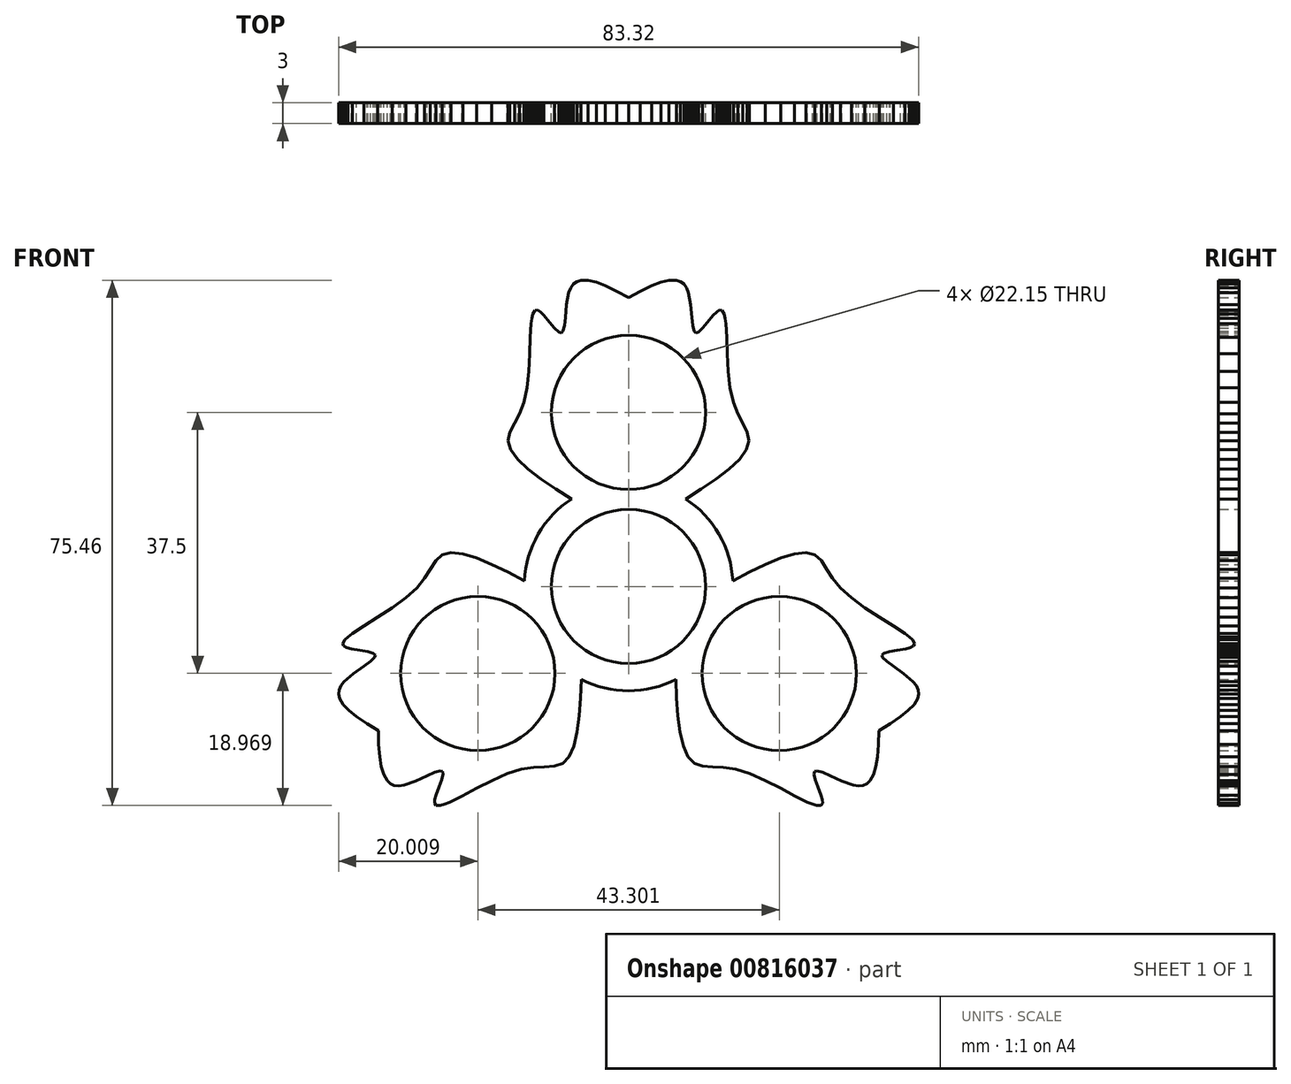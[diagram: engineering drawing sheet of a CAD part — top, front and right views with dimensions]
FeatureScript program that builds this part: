
annotation { "Feature Type Name" : "Feature", "Feature Type Description" : "" }
export const myFeature = defineFeature(function(context is Context, id is Id, definition is map)
    precondition{}
    {
        {
            var Q0;
            Q0=qCreatedBy(makeId("Front.planeOp"),FACE);
            var sketch = newSketch(context, id + "F0", { "sketchPlane" : qUnion([Q0])});
            skArc(sketch, "E0", {"start": v(0, -17.34) * mm, "mid": v(9.6, -11.8) * mm, "end": v(9.6, -0.72) * mm});
            skArc(sketch, "E1", {"start": v(9.6, -0.72) * mm, "mid": v(0, 4.81) * mm, "end": v(-9.6, -0.72) * mm});
            skArc(sketch, "E2", {"start": v(-9.6, -0.72) * mm, "mid": v(-9.6, -11.8) * mm, "end": v(0, -17.34) * mm});
            skLineSegment(sketch, "E3", {"start": v(0, 35.24) * mm, "end": v(-1.7, 36.16) * mm});
            skLineSegment(sketch, "E4", {"start": v(-1.7, 36.16) * mm, "end": v(-3.34, 36.95) * mm});
            skLineSegment(sketch, "E5", {"start": v(-3.34, 36.95) * mm, "end": v(-4.64, 37.45) * mm});
            skLineSegment(sketch, "E6", {"start": v(-4.64, 37.45) * mm, "end": v(-5.82, 37.73) * mm});
            skLineSegment(sketch, "E7", {"start": v(-5.82, 37.73) * mm, "end": v(-6.85, 37.73) * mm});
            skLineSegment(sketch, "E8", {"start": v(-6.85, 37.73) * mm, "end": v(-7.44, 37.55) * mm});
            skLineSegment(sketch, "E9", {"start": v(-7.44, 37.55) * mm, "end": v(-7.93, 37.2) * mm});
            skLineSegment(sketch, "E10", {"start": v(-7.93, 37.2) * mm, "end": v(-8.3, 36.67) * mm});
            skLineSegment(sketch, "E11", {"start": v(-8.3, 36.67) * mm, "end": v(-8.59, 35.96) * mm});
            skLineSegment(sketch, "E12", {"start": v(-8.59, 35.96) * mm, "end": v(-8.92, 34.22) * mm});
            skLineSegment(sketch, "E13", {"start": v(-8.92, 34.22) * mm, "end": v(-9.08, 32.4) * mm});
            skLineSegment(sketch, "E14", {"start": v(-9.08, 32.4) * mm, "end": v(-9.2, 31.24) * mm});
            skLineSegment(sketch, "E15", {"start": v(-9.2, 31.24) * mm, "end": v(-9.41, 30.44) * mm});
            skLineSegment(sketch, "E16", {"start": v(-9.41, 30.44) * mm, "end": v(-9.66, 30.18) * mm});
            skLineSegment(sketch, "E17", {"start": v(-9.66, 30.18) * mm, "end": v(-10.02, 30.29) * mm});
            skLineSegment(sketch, "E18", {"start": v(-10.02, 30.29) * mm, "end": v(-10.64, 30.86) * mm});
            skLineSegment(sketch, "E19", {"start": v(-10.64, 30.86) * mm, "end": v(-11.34, 31.71) * mm});
            skLineSegment(sketch, "E20", {"start": v(-11.34, 31.71) * mm, "end": v(-12.15, 32.69) * mm});
            skLineSegment(sketch, "E21", {"start": v(-12.15, 32.69) * mm, "end": v(-12.63, 33.18) * mm});
            skLineSegment(sketch, "E22", {"start": v(-12.63, 33.18) * mm, "end": v(-13.05, 33.45) * mm});
            skLineSegment(sketch, "E23", {"start": v(-13.05, 33.45) * mm, "end": v(-13.41, 33.42) * mm});
            skLineSegment(sketch, "E24", {"start": v(-13.41, 33.42) * mm, "end": v(-13.75, 32.88) * mm});
            skLineSegment(sketch, "E25", {"start": v(-13.75, 32.88) * mm, "end": v(-13.9, 32.27) * mm});
            skLineSegment(sketch, "E26", {"start": v(-13.9, 32.27) * mm, "end": v(-14, 31.5) * mm});
            skLineSegment(sketch, "E27", {"start": v(-14, 31.5) * mm, "end": v(-14.12, 29.5) * mm});
            skLineSegment(sketch, "E28", {"start": v(-14.12, 29.5) * mm, "end": v(-14.2, 27.15) * mm});
            skLineSegment(sketch, "E29", {"start": v(-14.2, 27.15) * mm, "end": v(-14.33, 24.67) * mm});
            skLineSegment(sketch, "E30", {"start": v(-14.33, 24.67) * mm, "end": v(-14.58, 22.27) * mm});
            skLineSegment(sketch, "E31", {"start": v(-14.58, 22.27) * mm, "end": v(-15.04, 20.2) * mm});
            skLineSegment(sketch, "E32", {"start": v(-15.04, 20.2) * mm, "end": v(-15.69, 18.53) * mm});
            skLineSegment(sketch, "E33", {"start": v(-15.69, 18.53) * mm, "end": v(-16.38, 17.18) * mm});
            skLineSegment(sketch, "E34", {"start": v(-16.38, 17.18) * mm, "end": v(-17.04, 15.86) * mm});
            skLineSegment(sketch, "E35", {"start": v(-17.04, 15.86) * mm, "end": v(-17.3, 14.65) * mm});
            skLineSegment(sketch, "E36", {"start": v(-17.3, 14.65) * mm, "end": v(-16.94, 13.38) * mm});
            skLineSegment(sketch, "E37", {"start": v(-16.94, 13.38) * mm, "end": v(-15.94, 12.03) * mm});
            skLineSegment(sketch, "E38", {"start": v(-15.94, 12.03) * mm, "end": v(-14.44, 10.61) * mm});
            skLineSegment(sketch, "E39", {"start": v(-14.44, 10.61) * mm, "end": v(-12.56, 9.17) * mm});
            skLineSegment(sketch, "E40", {"start": v(-12.56, 9.17) * mm, "end": v(-10.43, 7.72) * mm});
            skLineSegment(sketch, "E41", {"start": v(-10.43, 7.72) * mm, "end": v(-8.18, 6.31) * mm});
            skArc(sketch, "E42", {"start": v(-8.18, 6.31) * mm, "mid": v(-10.88, 4.06) * mm, "end": v(-13, 1.24) * mm});
            skArc(sketch, "E43", {"start": v(-13, 1.24) * mm, "mid": v(-14.38, -2) * mm, "end": v(-14.98, -5.47) * mm});
            skLineSegment(sketch, "E44", {"start": v(-14.98, -5.47) * mm, "end": v(-17.32, -4.22) * mm});
            skLineSegment(sketch, "E45", {"start": v(-17.32, -4.22) * mm, "end": v(-19.64, -3.1) * mm});
            skLineSegment(sketch, "E46", {"start": v(-19.64, -3.1) * mm, "end": v(-21.83, -2.2) * mm});
            skLineSegment(sketch, "E47", {"start": v(-21.83, -2.2) * mm, "end": v(-23.81, -1.6) * mm});
            skLineSegment(sketch, "E48", {"start": v(-23.81, -1.6) * mm, "end": v(-25.48, -1.41) * mm});
            skLineSegment(sketch, "E49", {"start": v(-25.48, -1.41) * mm, "end": v(-26.76, -1.73) * mm});
            skLineSegment(sketch, "E50", {"start": v(-26.76, -1.73) * mm, "end": v(-27.67, -2.56) * mm});
            skLineSegment(sketch, "E51", {"start": v(-27.67, -2.56) * mm, "end": v(-28.49, -3.8) * mm});
            skLineSegment(sketch, "E52", {"start": v(-28.49, -3.8) * mm, "end": v(-29.31, -5.07) * mm});
            skLineSegment(sketch, "E53", {"start": v(-29.31, -5.07) * mm, "end": v(-30.43, -6.46) * mm});
            skLineSegment(sketch, "E54", {"start": v(-30.43, -6.46) * mm, "end": v(-32, -7.9) * mm});
            skLineSegment(sketch, "E55", {"start": v(-32, -7.9) * mm, "end": v(-33.95, -9.31) * mm});
            skLineSegment(sketch, "E56", {"start": v(-33.95, -9.31) * mm, "end": v(-36.04, -10.66) * mm});
            skLineSegment(sketch, "E57", {"start": v(-36.04, -10.66) * mm, "end": v(-38.04, -11.91) * mm});
            skLineSegment(sketch, "E58", {"start": v(-38.04, -11.91) * mm, "end": v(-39.7, -13.02) * mm});
            skLineSegment(sketch, "E59", {"start": v(-39.7, -13.02) * mm, "end": v(-40.31, -13.5) * mm});
            skLineSegment(sketch, "E60", {"start": v(-40.31, -13.5) * mm, "end": v(-40.77, -13.93) * mm});
            skLineSegment(sketch, "E61", {"start": v(-40.77, -13.93) * mm, "end": v(-41.07, -14.49) * mm});
            skLineSegment(sketch, "E62", {"start": v(-41.07, -14.49) * mm, "end": v(-40.92, -14.81) * mm});
            skLineSegment(sketch, "E63", {"start": v(-40.92, -14.81) * mm, "end": v(-40.47, -15.04) * mm});
            skLineSegment(sketch, "E64", {"start": v(-40.47, -15.04) * mm, "end": v(-39.8, -15.21) * mm});
            skLineSegment(sketch, "E65", {"start": v(-39.8, -15.21) * mm, "end": v(-38.56, -15.42) * mm});
            skLineSegment(sketch, "E66", {"start": v(-38.56, -15.42) * mm, "end": v(-37.47, -15.6) * mm});
            skLineSegment(sketch, "E67", {"start": v(-37.47, -15.6) * mm, "end": v(-36.66, -15.85) * mm});
            skLineSegment(sketch, "E68", {"start": v(-36.66, -15.85) * mm, "end": v(-36.4, -16.11) * mm});
            skLineSegment(sketch, "E69", {"start": v(-36.4, -16.11) * mm, "end": v(-36.49, -16.46) * mm});
            skLineSegment(sketch, "E70", {"start": v(-36.49, -16.46) * mm, "end": v(-37.08, -17.04) * mm});
            skLineSegment(sketch, "E71", {"start": v(-37.08, -17.04) * mm, "end": v(-38.03, -17.73) * mm});
            skLineSegment(sketch, "E72", {"start": v(-38.03, -17.73) * mm, "end": v(-39.52, -18.78) * mm});
            skLineSegment(sketch, "E73", {"start": v(-39.52, -18.78) * mm, "end": v(-40.86, -19.93) * mm});
            skLineSegment(sketch, "E74", {"start": v(-40.86, -19.93) * mm, "end": v(-41.33, -20.53) * mm});
            skLineSegment(sketch, "E75", {"start": v(-41.33, -20.53) * mm, "end": v(-41.6, -21.13) * mm});
            skLineSegment(sketch, "E76", {"start": v(-41.6, -21.13) * mm, "end": v(-41.66, -21.73) * mm});
            skLineSegment(sketch, "E77", {"start": v(-41.66, -21.73) * mm, "end": v(-41.52, -22.32) * mm});
            skLineSegment(sketch, "E78", {"start": v(-41.52, -22.32) * mm, "end": v(-41, -23.21) * mm});
            skLineSegment(sketch, "E79", {"start": v(-41, -23.21) * mm, "end": v(-40.17, -24.1) * mm});
            skLineSegment(sketch, "E80", {"start": v(-40.17, -24.1) * mm, "end": v(-39.09, -24.98) * mm});
            skLineSegment(sketch, "E81", {"start": v(-39.09, -24.98) * mm, "end": v(-37.59, -26) * mm});
            skLineSegment(sketch, "E82", {"start": v(-37.59, -26) * mm, "end": v(-35.94, -27.01) * mm});
            skLineSegment(sketch, "E83", {"start": v(-35.94, -27.01) * mm, "end": v(-35.89, -28.94) * mm});
            skLineSegment(sketch, "E84", {"start": v(-35.89, -28.94) * mm, "end": v(-35.75, -30.75) * mm});
            skLineSegment(sketch, "E85", {"start": v(-35.75, -30.75) * mm, "end": v(-35.53, -32.13) * mm});
            skLineSegment(sketch, "E86", {"start": v(-35.53, -32.13) * mm, "end": v(-35.18, -33.3) * mm});
            skLineSegment(sketch, "E87", {"start": v(-35.18, -33.3) * mm, "end": v(-34.67, -34.2) * mm});
            skLineSegment(sketch, "E88", {"start": v(-34.67, -34.2) * mm, "end": v(-34.22, -34.6) * mm});
            skLineSegment(sketch, "E89", {"start": v(-34.22, -34.6) * mm, "end": v(-33.68, -34.86) * mm});
            skLineSegment(sketch, "E90", {"start": v(-33.68, -34.86) * mm, "end": v(-33.02, -34.92) * mm});
            skLineSegment(sketch, "E91", {"start": v(-33.02, -34.92) * mm, "end": v(-32.27, -34.8) * mm});
            skLineSegment(sketch, "E92", {"start": v(-32.27, -34.8) * mm, "end": v(-30.6, -34.22) * mm});
            skLineSegment(sketch, "E93", {"start": v(-30.6, -34.22) * mm, "end": v(-28.94, -33.46) * mm});
            skLineSegment(sketch, "E94", {"start": v(-28.94, -33.46) * mm, "end": v(-27.87, -32.99) * mm});
            skLineSegment(sketch, "E95", {"start": v(-27.87, -32.99) * mm, "end": v(-27.08, -32.76) * mm});
            skLineSegment(sketch, "E96", {"start": v(-27.08, -32.76) * mm, "end": v(-26.73, -32.85) * mm});
            skLineSegment(sketch, "E97", {"start": v(-26.73, -32.85) * mm, "end": v(-26.64, -33.21) * mm});
            skLineSegment(sketch, "E98", {"start": v(-26.64, -33.21) * mm, "end": v(-26.83, -34.03) * mm});
            skLineSegment(sketch, "E99", {"start": v(-26.83, -34.03) * mm, "end": v(-27.21, -35.07) * mm});
            skLineSegment(sketch, "E100", {"start": v(-27.21, -35.07) * mm, "end": v(-27.66, -36.26) * mm});
            skLineSegment(sketch, "E101", {"start": v(-27.66, -36.26) * mm, "end": v(-27.84, -36.92) * mm});
            skLineSegment(sketch, "E102", {"start": v(-27.84, -36.92) * mm, "end": v(-27.86, -37.42) * mm});
            skLineSegment(sketch, "E103", {"start": v(-27.86, -37.42) * mm, "end": v(-27.66, -37.72) * mm});
            skLineSegment(sketch, "E104", {"start": v(-27.66, -37.72) * mm, "end": v(-27.02, -37.73) * mm});
            skLineSegment(sketch, "E105", {"start": v(-27.02, -37.73) * mm, "end": v(-26.42, -37.56) * mm});
            skLineSegment(sketch, "E106", {"start": v(-26.42, -37.56) * mm, "end": v(-25.7, -37.26) * mm});
            skLineSegment(sketch, "E107", {"start": v(-25.7, -37.26) * mm, "end": v(-23.91, -36.38) * mm});
            skLineSegment(sketch, "E108", {"start": v(-23.91, -36.38) * mm, "end": v(-21.83, -35.27) * mm});
            skLineSegment(sketch, "E109", {"start": v(-21.83, -35.27) * mm, "end": v(-19.62, -34.14) * mm});
            skLineSegment(sketch, "E110", {"start": v(-19.62, -34.14) * mm, "end": v(-17.42, -33.16) * mm});
            skLineSegment(sketch, "E111", {"start": v(-17.42, -33.16) * mm, "end": v(-15.4, -32.51) * mm});
            skLineSegment(sketch, "E112", {"start": v(-15.4, -32.51) * mm, "end": v(-13.62, -32.24) * mm});
            skLineSegment(sketch, "E113", {"start": v(-13.62, -32.24) * mm, "end": v(-12.1, -32.16) * mm});
            skLineSegment(sketch, "E114", {"start": v(-12.1, -32.16) * mm, "end": v(-10.63, -32.08) * mm});
            skLineSegment(sketch, "E115", {"start": v(-10.63, -32.08) * mm, "end": v(-9.45, -31.7) * mm});
            skLineSegment(sketch, "E116", {"start": v(-9.45, -31.7) * mm, "end": v(-8.54, -30.75) * mm});
            skLineSegment(sketch, "E117", {"start": v(-8.54, -30.75) * mm, "end": v(-7.87, -29.21) * mm});
            skLineSegment(sketch, "E118", {"start": v(-7.87, -29.21) * mm, "end": v(-7.4, -27.2) * mm});
            skLineSegment(sketch, "E119", {"start": v(-7.4, -27.2) * mm, "end": v(-7.08, -24.85) * mm});
            skLineSegment(sketch, "E120", {"start": v(-7.08, -24.85) * mm, "end": v(-6.9, -22.28) * mm});
            skLineSegment(sketch, "E121", {"start": v(-6.9, -22.28) * mm, "end": v(-6.8, -19.63) * mm});
            skArc(sketch, "E122", {"start": v(-6.8, -19.63) * mm, "mid": v(-3.5, -20.85) * mm, "end": v(0, -21.26) * mm});
            skArc(sketch, "E123", {"start": v(0, -21.26) * mm, "mid": v(3.5, -20.85) * mm, "end": v(6.8, -19.63) * mm});
            skLineSegment(sketch, "E124", {"start": v(6.8, -19.63) * mm, "end": v(6.9, -22.28) * mm});
            skLineSegment(sketch, "E125", {"start": v(6.9, -22.28) * mm, "end": v(7.08, -24.85) * mm});
            skLineSegment(sketch, "E126", {"start": v(7.08, -24.85) * mm, "end": v(7.4, -27.2) * mm});
            skLineSegment(sketch, "E127", {"start": v(7.4, -27.2) * mm, "end": v(7.87, -29.21) * mm});
            skLineSegment(sketch, "E128", {"start": v(7.87, -29.21) * mm, "end": v(8.54, -30.75) * mm});
            skLineSegment(sketch, "E129", {"start": v(8.54, -30.75) * mm, "end": v(9.45, -31.7) * mm});
            skLineSegment(sketch, "E130", {"start": v(9.45, -31.7) * mm, "end": v(10.63, -32.08) * mm});
            skLineSegment(sketch, "E131", {"start": v(10.63, -32.08) * mm, "end": v(12.1, -32.16) * mm});
            skLineSegment(sketch, "E132", {"start": v(12.1, -32.16) * mm, "end": v(13.62, -32.24) * mm});
            skLineSegment(sketch, "E133", {"start": v(13.62, -32.24) * mm, "end": v(15.4, -32.51) * mm});
            skLineSegment(sketch, "E134", {"start": v(15.4, -32.51) * mm, "end": v(17.42, -33.16) * mm});
            skLineSegment(sketch, "E135", {"start": v(17.42, -33.16) * mm, "end": v(19.62, -34.14) * mm});
            skLineSegment(sketch, "E136", {"start": v(19.62, -34.14) * mm, "end": v(21.83, -35.27) * mm});
            skLineSegment(sketch, "E137", {"start": v(21.83, -35.27) * mm, "end": v(23.91, -36.38) * mm});
            skLineSegment(sketch, "E138", {"start": v(23.91, -36.38) * mm, "end": v(25.7, -37.26) * mm});
            skLineSegment(sketch, "E139", {"start": v(25.7, -37.26) * mm, "end": v(26.42, -37.56) * mm});
            skLineSegment(sketch, "E140", {"start": v(26.42, -37.56) * mm, "end": v(27.02, -37.73) * mm});
            skLineSegment(sketch, "E141", {"start": v(27.02, -37.73) * mm, "end": v(27.66, -37.72) * mm});
            skLineSegment(sketch, "E142", {"start": v(27.66, -37.72) * mm, "end": v(27.86, -37.42) * mm});
            skLineSegment(sketch, "E143", {"start": v(27.86, -37.42) * mm, "end": v(27.84, -36.92) * mm});
            skLineSegment(sketch, "E144", {"start": v(27.84, -36.92) * mm, "end": v(27.66, -36.26) * mm});
            skLineSegment(sketch, "E145", {"start": v(27.66, -36.26) * mm, "end": v(27.21, -35.07) * mm});
            skLineSegment(sketch, "E146", {"start": v(27.21, -35.07) * mm, "end": v(26.83, -34.03) * mm});
            skLineSegment(sketch, "E147", {"start": v(26.83, -34.03) * mm, "end": v(26.64, -33.21) * mm});
            skLineSegment(sketch, "E148", {"start": v(26.64, -33.21) * mm, "end": v(26.73, -32.85) * mm});
            skLineSegment(sketch, "E149", {"start": v(26.73, -32.85) * mm, "end": v(27.08, -32.76) * mm});
            skLineSegment(sketch, "E150", {"start": v(27.08, -32.76) * mm, "end": v(27.87, -32.99) * mm});
            skLineSegment(sketch, "E151", {"start": v(27.87, -32.99) * mm, "end": v(28.94, -33.46) * mm});
            skLineSegment(sketch, "E152", {"start": v(28.94, -33.46) * mm, "end": v(30.6, -34.22) * mm});
            skLineSegment(sketch, "E153", {"start": v(30.6, -34.22) * mm, "end": v(32.27, -34.8) * mm});
            skLineSegment(sketch, "E154", {"start": v(32.27, -34.8) * mm, "end": v(33.02, -34.92) * mm});
            skLineSegment(sketch, "E155", {"start": v(33.02, -34.92) * mm, "end": v(33.68, -34.86) * mm});
            skLineSegment(sketch, "E156", {"start": v(33.68, -34.86) * mm, "end": v(34.22, -34.6) * mm});
            skLineSegment(sketch, "E157", {"start": v(34.22, -34.6) * mm, "end": v(34.67, -34.2) * mm});
            skLineSegment(sketch, "E158", {"start": v(34.67, -34.2) * mm, "end": v(35.18, -33.3) * mm});
            skLineSegment(sketch, "E159", {"start": v(35.18, -33.3) * mm, "end": v(35.53, -32.13) * mm});
            skLineSegment(sketch, "E160", {"start": v(35.53, -32.13) * mm, "end": v(35.75, -30.75) * mm});
            skLineSegment(sketch, "E161", {"start": v(35.75, -30.75) * mm, "end": v(35.89, -28.94) * mm});
            skLineSegment(sketch, "E162", {"start": v(35.89, -28.94) * mm, "end": v(35.94, -27.01) * mm});
            skLineSegment(sketch, "E163", {"start": v(35.94, -27.01) * mm, "end": v(37.59, -26) * mm});
            skLineSegment(sketch, "E164", {"start": v(37.59, -26) * mm, "end": v(39.09, -24.98) * mm});
            skLineSegment(sketch, "E165", {"start": v(39.09, -24.98) * mm, "end": v(40.17, -24.1) * mm});
            skLineSegment(sketch, "E166", {"start": v(40.17, -24.1) * mm, "end": v(41, -23.21) * mm});
            skLineSegment(sketch, "E167", {"start": v(41, -23.21) * mm, "end": v(41.52, -22.32) * mm});
            skLineSegment(sketch, "E168", {"start": v(41.52, -22.32) * mm, "end": v(41.66, -21.73) * mm});
            skLineSegment(sketch, "E169", {"start": v(41.66, -21.73) * mm, "end": v(41.6, -21.13) * mm});
            skLineSegment(sketch, "E170", {"start": v(41.6, -21.13) * mm, "end": v(41.33, -20.53) * mm});
            skLineSegment(sketch, "E171", {"start": v(41.33, -20.53) * mm, "end": v(40.86, -19.93) * mm});
            skLineSegment(sketch, "E172", {"start": v(40.86, -19.93) * mm, "end": v(39.52, -18.78) * mm});
            skLineSegment(sketch, "E173", {"start": v(39.52, -18.78) * mm, "end": v(38.03, -17.73) * mm});
            skLineSegment(sketch, "E174", {"start": v(38.03, -17.73) * mm, "end": v(37.08, -17.04) * mm});
            skLineSegment(sketch, "E175", {"start": v(37.08, -17.04) * mm, "end": v(36.49, -16.46) * mm});
            skLineSegment(sketch, "E176", {"start": v(36.49, -16.46) * mm, "end": v(36.4, -16.11) * mm});
            skLineSegment(sketch, "E177", {"start": v(36.4, -16.11) * mm, "end": v(36.66, -15.85) * mm});
            skLineSegment(sketch, "E178", {"start": v(36.66, -15.85) * mm, "end": v(37.47, -15.6) * mm});
            skLineSegment(sketch, "E179", {"start": v(37.47, -15.6) * mm, "end": v(38.56, -15.42) * mm});
            skLineSegment(sketch, "E180", {"start": v(38.56, -15.42) * mm, "end": v(39.8, -15.21) * mm});
            skLineSegment(sketch, "E181", {"start": v(39.8, -15.21) * mm, "end": v(40.47, -15.04) * mm});
            skLineSegment(sketch, "E182", {"start": v(40.47, -15.04) * mm, "end": v(40.92, -14.81) * mm});
            skLineSegment(sketch, "E183", {"start": v(40.92, -14.81) * mm, "end": v(41.07, -14.49) * mm});
            skLineSegment(sketch, "E184", {"start": v(41.07, -14.49) * mm, "end": v(40.77, -13.93) * mm});
            skLineSegment(sketch, "E185", {"start": v(40.77, -13.93) * mm, "end": v(40.31, -13.5) * mm});
            skLineSegment(sketch, "E186", {"start": v(40.31, -13.5) * mm, "end": v(39.7, -13.02) * mm});
            skLineSegment(sketch, "E187", {"start": v(39.7, -13.02) * mm, "end": v(38.04, -11.91) * mm});
            skLineSegment(sketch, "E188", {"start": v(38.04, -11.91) * mm, "end": v(36.04, -10.66) * mm});
            skLineSegment(sketch, "E189", {"start": v(36.04, -10.66) * mm, "end": v(33.95, -9.31) * mm});
            skLineSegment(sketch, "E190", {"start": v(33.95, -9.31) * mm, "end": v(32, -7.9) * mm});
            skLineSegment(sketch, "E191", {"start": v(32, -7.9) * mm, "end": v(30.43, -6.46) * mm});
            skLineSegment(sketch, "E192", {"start": v(30.43, -6.46) * mm, "end": v(29.31, -5.07) * mm});
            skLineSegment(sketch, "E193", {"start": v(29.31, -5.07) * mm, "end": v(28.49, -3.8) * mm});
            skLineSegment(sketch, "E194", {"start": v(28.49, -3.8) * mm, "end": v(27.67, -2.56) * mm});
            skLineSegment(sketch, "E195", {"start": v(27.67, -2.56) * mm, "end": v(26.76, -1.73) * mm});
            skLineSegment(sketch, "E196", {"start": v(26.76, -1.73) * mm, "end": v(25.48, -1.41) * mm});
            skLineSegment(sketch, "E197", {"start": v(25.48, -1.41) * mm, "end": v(23.81, -1.6) * mm});
            skLineSegment(sketch, "E198", {"start": v(23.81, -1.6) * mm, "end": v(21.83, -2.2) * mm});
            skLineSegment(sketch, "E199", {"start": v(21.83, -2.2) * mm, "end": v(19.64, -3.1) * mm});
            skLineSegment(sketch, "E200", {"start": v(19.64, -3.1) * mm, "end": v(17.32, -4.22) * mm});
            skLineSegment(sketch, "E201", {"start": v(17.32, -4.22) * mm, "end": v(14.98, -5.47) * mm});
            skArc(sketch, "E202", {"start": v(14.98, -5.47) * mm, "mid": v(14.38, -2) * mm, "end": v(13, 1.24) * mm});
            skArc(sketch, "E203", {"start": v(13, 1.24) * mm, "mid": v(10.88, 4.06) * mm, "end": v(8.18, 6.31) * mm});
            skLineSegment(sketch, "E204", {"start": v(8.18, 6.31) * mm, "end": v(10.43, 7.72) * mm});
            skLineSegment(sketch, "E205", {"start": v(10.43, 7.72) * mm, "end": v(12.56, 9.17) * mm});
            skLineSegment(sketch, "E206", {"start": v(12.56, 9.17) * mm, "end": v(14.44, 10.61) * mm});
            skLineSegment(sketch, "E207", {"start": v(14.44, 10.61) * mm, "end": v(15.94, 12.03) * mm});
            skLineSegment(sketch, "E208", {"start": v(15.94, 12.03) * mm, "end": v(16.94, 13.38) * mm});
            skLineSegment(sketch, "E209", {"start": v(16.94, 13.38) * mm, "end": v(17.3, 14.65) * mm});
            skLineSegment(sketch, "E210", {"start": v(17.3, 14.65) * mm, "end": v(17.04, 15.86) * mm});
            skLineSegment(sketch, "E211", {"start": v(17.04, 15.86) * mm, "end": v(16.38, 17.18) * mm});
            skLineSegment(sketch, "E212", {"start": v(16.38, 17.18) * mm, "end": v(15.69, 18.53) * mm});
            skLineSegment(sketch, "E213", {"start": v(15.69, 18.53) * mm, "end": v(15.04, 20.2) * mm});
            skLineSegment(sketch, "E214", {"start": v(15.04, 20.2) * mm, "end": v(14.58, 22.27) * mm});
            skLineSegment(sketch, "E215", {"start": v(14.58, 22.27) * mm, "end": v(14.33, 24.67) * mm});
            skLineSegment(sketch, "E216", {"start": v(14.33, 24.67) * mm, "end": v(14.2, 27.15) * mm});
            skLineSegment(sketch, "E217", {"start": v(14.2, 27.15) * mm, "end": v(14.12, 29.5) * mm});
            skLineSegment(sketch, "E218", {"start": v(14.12, 29.5) * mm, "end": v(14, 31.5) * mm});
            skLineSegment(sketch, "E219", {"start": v(14, 31.5) * mm, "end": v(13.9, 32.27) * mm});
            skLineSegment(sketch, "E220", {"start": v(13.9, 32.27) * mm, "end": v(13.75, 32.88) * mm});
            skLineSegment(sketch, "E221", {"start": v(13.75, 32.88) * mm, "end": v(13.41, 33.42) * mm});
            skLineSegment(sketch, "E222", {"start": v(13.41, 33.42) * mm, "end": v(13.05, 33.45) * mm});
            skLineSegment(sketch, "E223", {"start": v(13.05, 33.45) * mm, "end": v(12.63, 33.18) * mm});
            skLineSegment(sketch, "E224", {"start": v(12.63, 33.18) * mm, "end": v(12.15, 32.69) * mm});
            skLineSegment(sketch, "E225", {"start": v(12.15, 32.69) * mm, "end": v(11.34, 31.71) * mm});
            skLineSegment(sketch, "E226", {"start": v(11.34, 31.71) * mm, "end": v(10.64, 30.86) * mm});
            skLineSegment(sketch, "E227", {"start": v(10.64, 30.86) * mm, "end": v(10.02, 30.29) * mm});
            skLineSegment(sketch, "E228", {"start": v(10.02, 30.29) * mm, "end": v(9.66, 30.18) * mm});
            skLineSegment(sketch, "E229", {"start": v(9.66, 30.18) * mm, "end": v(9.41, 30.44) * mm});
            skLineSegment(sketch, "E230", {"start": v(9.41, 30.44) * mm, "end": v(9.2, 31.24) * mm});
            skLineSegment(sketch, "E231", {"start": v(9.2, 31.24) * mm, "end": v(9.08, 32.4) * mm});
            skLineSegment(sketch, "E232", {"start": v(9.08, 32.4) * mm, "end": v(8.92, 34.22) * mm});
            skLineSegment(sketch, "E233", {"start": v(8.92, 34.22) * mm, "end": v(8.59, 35.96) * mm});
            skLineSegment(sketch, "E234", {"start": v(8.59, 35.96) * mm, "end": v(8.3, 36.67) * mm});
            skLineSegment(sketch, "E235", {"start": v(8.3, 36.67) * mm, "end": v(7.93, 37.2) * mm});
            skLineSegment(sketch, "E236", {"start": v(7.93, 37.2) * mm, "end": v(7.44, 37.55) * mm});
            skLineSegment(sketch, "E237", {"start": v(7.44, 37.55) * mm, "end": v(6.85, 37.73) * mm});
            skLineSegment(sketch, "E238", {"start": v(6.85, 37.73) * mm, "end": v(5.82, 37.73) * mm});
            skLineSegment(sketch, "E239", {"start": v(5.82, 37.73) * mm, "end": v(4.64, 37.45) * mm});
            skLineSegment(sketch, "E240", {"start": v(4.64, 37.45) * mm, "end": v(3.34, 36.95) * mm});
            skLineSegment(sketch, "E241", {"start": v(3.34, 36.95) * mm, "end": v(1.7, 36.16) * mm});
            skLineSegment(sketch, "E242", {"start": v(1.7, 36.16) * mm, "end": v(0, 35.24) * mm});
            skCircle(sketch, "E243", {"center": v(21.65, -18.76) * mm, "radius": 11.07 * mm});
            skCircle(sketch, "E244", {"center": v(-21.65, -18.76) * mm, "radius": 11.07 * mm});
            skCircle(sketch, "E245", {"center": v(0, 18.74) * mm, "radius": 11.07 * mm});
            skSolve(sketch);
        }
        {
            var Q0;
            Q0 = qSketchRegion(id + "F0", true);
            extrude(context, id + "F1", {"entities" : qUnion([Q0]), "depth" : 3 * mm, "offsetDistance" : 25 * mm});
        }
    });
